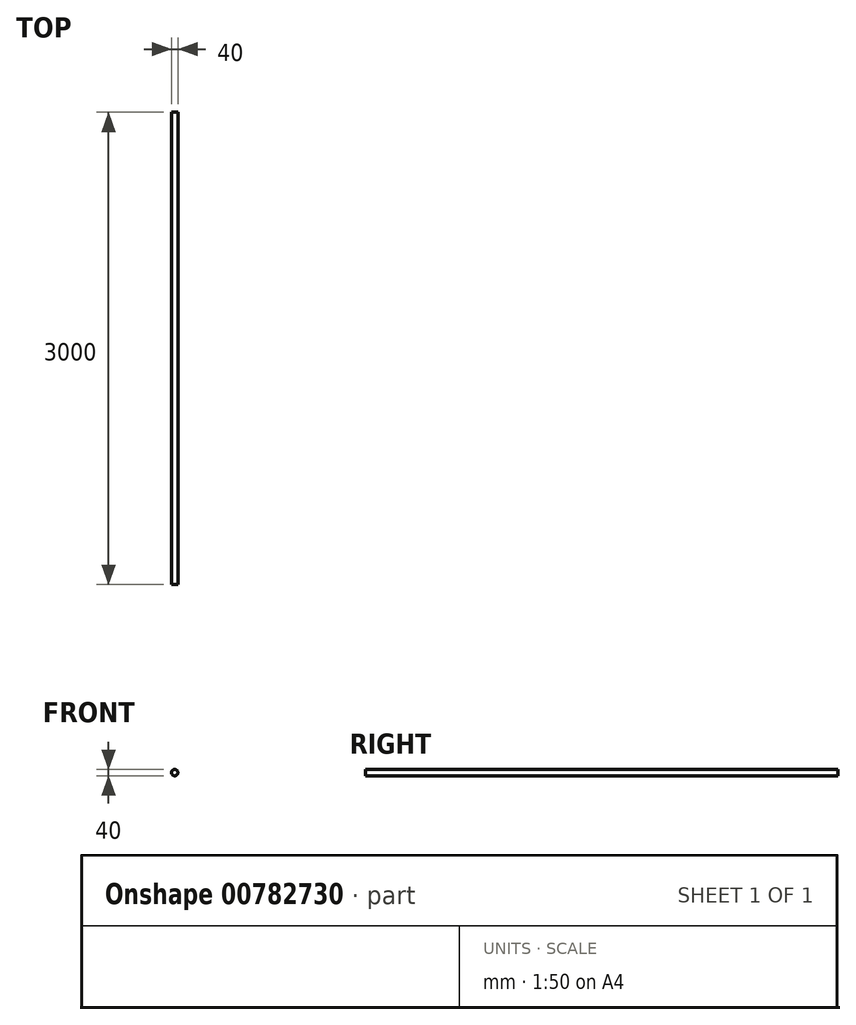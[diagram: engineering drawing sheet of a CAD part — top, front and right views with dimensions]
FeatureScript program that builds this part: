
annotation { "Feature Type Name" : "Feature", "Feature Type Description" : "" }
export const myFeature = defineFeature(function(context is Context, id is Id, definition is map)
    precondition{}
    {
        {
            var Q0;
            Q0=qCreatedBy(makeId("Front.planeOp"),FACE);
            var sketch = newSketch(context, id + "F0", { "sketchPlane" : qUnion([Q0])});
            skCircle(sketch, "E0", {"center": v(0, 0) * mm, "radius": 20 * mm});
            skSolve(sketch);
        }
        {
            var Q0;
            Q0 = qSketchRegion(id + "F0", true);
            extrude(context, id + "F1", {"entities" : qUnion([Q0]), "depth" : 3000 * mm, "offsetDistance" : 25 * mm});
        }
    });
